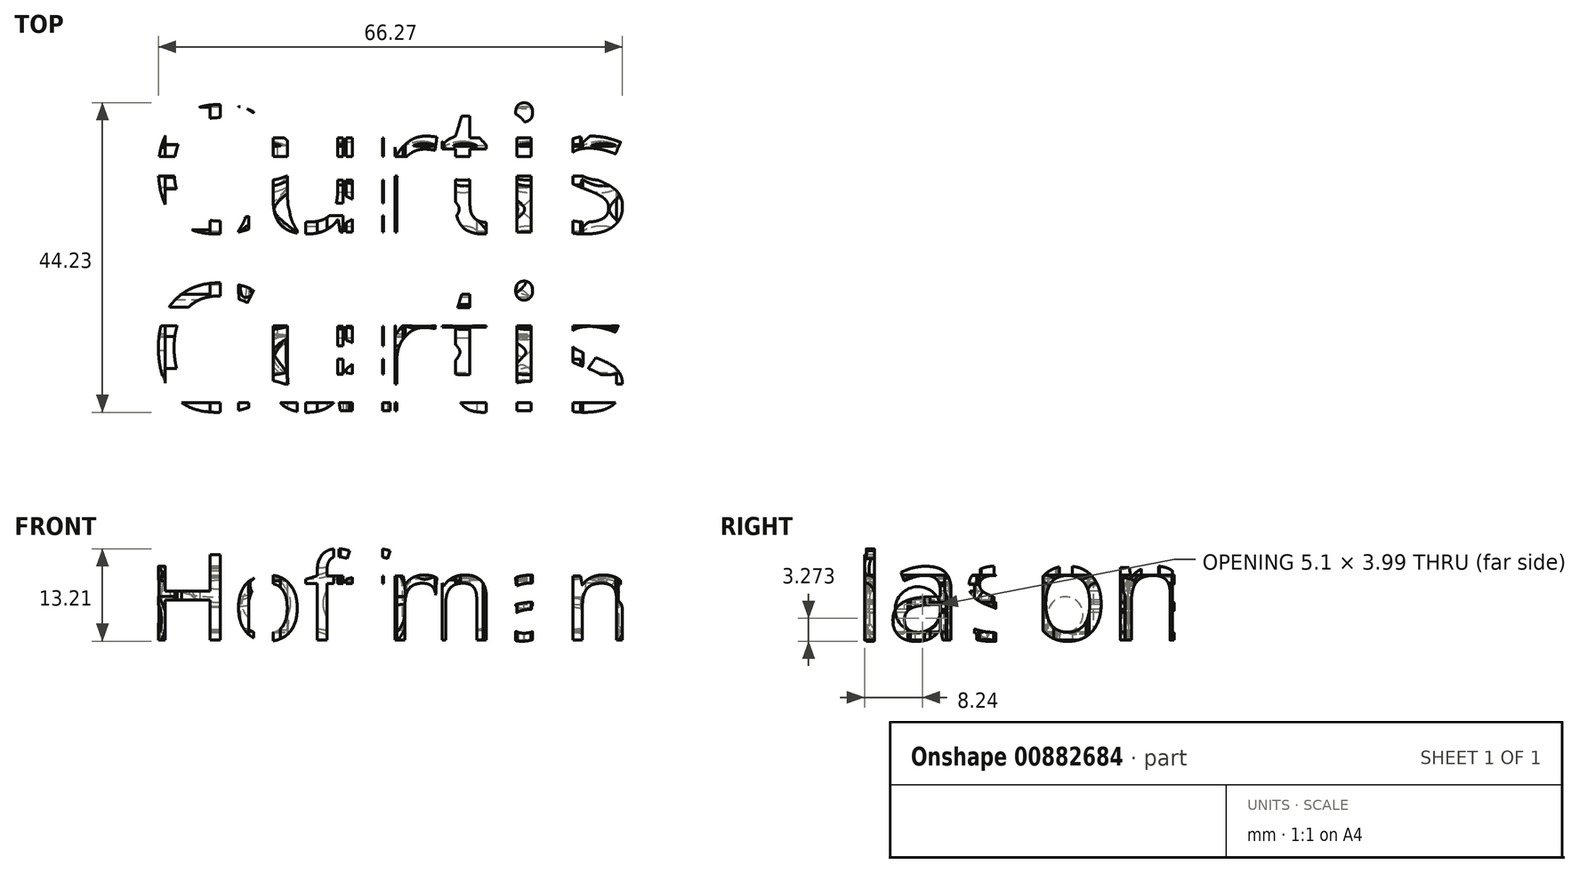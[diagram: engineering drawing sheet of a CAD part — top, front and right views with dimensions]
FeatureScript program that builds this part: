
annotation { "Feature Type Name" : "Feature", "Feature Type Description" : "" }
export const myFeature = defineFeature(function(context is Context, id is Id, definition is map)
    precondition{}
    {
        {
            var Q0;
            Q0=qCreatedBy(makeId("Right.planeOp"),FACE);
            var sketch = newSketch(context, id + "F0", { "sketchPlane" : qUnion([Q0])});
            skPoint(sketch, "E0", {"position": v(10, 10) * mm});
            skText(sketch, "E1", { "text": "Jason\n", "fontName": "OpenSans-Regular.ttf"});
            const initialGuessF0  = {"E1": [0.01, 0.01, 1, 0, 0.01395]};
            skSetInitialGuess(sketch, initialGuessF0);
            skSolve(sketch);
        }
        {
            var Q0;
            Q0=qCreatedBy(makeId("Front.planeOp"),FACE);
            var sketch = newSketch(context, id + "F1", { "sketchPlane" : qUnion([Q0])});
            skPoint(sketch, "E2", {"position": v(-10, 10) * mm});
            skText(sketch, "E3", { "text": "Hoffman", "fontName": "OpenSans-Regular.ttf"});
            const initialGuessF1  = {"E3": [-0.08, 0.01, 1, 0, 0.01228]};
            skSetInitialGuess(sketch, initialGuessF1);
            skSolve(sketch);
        }
        {
            var Q0;
            Q0 = qSketchRegion(id + "F0", true);
            extrude(context, id + "F2", {"entities" : qUnion([Q0]), "oppositeDirection" : true, "depth" : 80 * mm, "offsetDistance" : 25 * mm});
        }
        {
            var Q0;
            Q0 = qSketchRegion(id + "F1", true);
            extrude(context, id + "F3", {"entities" : qUnion([Q0]), "operationType" : NewBodyOperationType.INTERSECT, "oppositeDirection" : true, "depth" : 60 * mm, "offsetDistance" : 25 * mm});
        }
        {
            var Q0;
            Q0=qCreatedBy(makeId("Top.planeOp"),FACE);
            var sketch = newSketch(context, id + "F4", { "sketchPlane" : qUnion([Q0])});
            skPoint(sketch, "E4", {"position": v(-10, 12.27) * mm});
            skText(sketch, "E5", { "text": "Curtis\n", "fontName": "OpenSans-Regular.ttf"});
            skText(sketch, "E6", { "text": "Curtis", "fontName": "OpenSans-Regular.ttf"});
            const initialGuessF4  = {"E5": [-0.07944, 0.01227, 1, 0, 0.01815], "E6": [-0.07944, 0.03775, 1, 0, 0.01815]};
            skSetInitialGuess(sketch, initialGuessF4);
            skSolve(sketch);
        }
        {
            var Q0;
            Q0 = qSketchRegion(id + "F4", true);
            extrude(context, id + "F5", {"entities" : qUnion([Q0]), "operationType" : NewBodyOperationType.INTERSECT, "depth" : 25 * mm, "offsetDistance" : 25 * mm});
        }
    });
